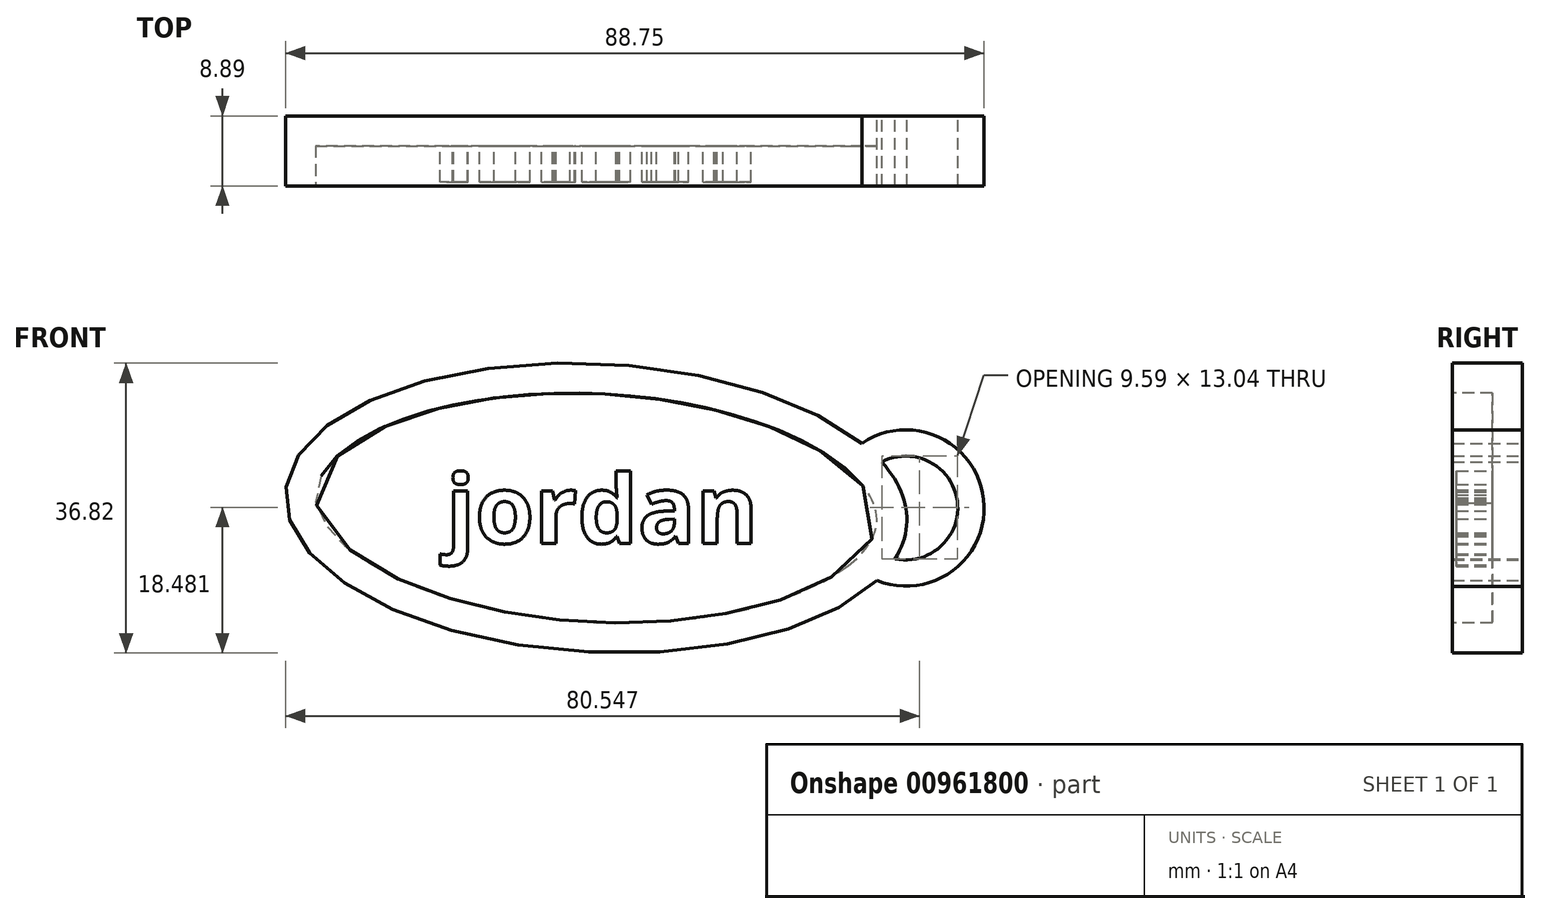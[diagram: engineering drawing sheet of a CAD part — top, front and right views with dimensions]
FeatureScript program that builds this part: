
annotation { "Feature Type Name" : "Feature", "Feature Type Description" : "" }
export const myFeature = defineFeature(function(context is Context, id is Id, definition is map)
    precondition{}
    {
        {
            var Q0;
            Q0=qCreatedBy(makeId("Front.planeOp"),FACE);
            var sketch = newSketch(context, id + "F0", { "sketchPlane" : qUnion([Q0])});
            skEllipticalArc(sketch, "E0", {});
            skArc(sketch, "E1", {"start": v(35.66, -9.23) * mm, "mid": v(49.22, 1.07) * mm, "end": v(33.76, 8.22) * mm});
            skArc(sketch, "E2", {"start": v(37.98, -6.45) * mm, "mid": v(45.87, 0.9) * mm, "end": v(36.28, 5.84) * mm});
            skEllipticalArc(sketch, "E3.trimOffspring", {});
            skFitSpline(sketch, "E4", {"points": [v(33.76, 8.22) * mm, v(36.28, 5.84) * mm], "startDerivative": vector(4.84, -3.4) * mm, "endDerivative": vector(4.84, -3.4) * mm});
            skFitSpline(sketch, "E5", {"points": [v(35.66, -9.23) * mm, v(37.98, -6.45) * mm], "startDerivative": vector(4.95, 3.83) * mm, "endDerivative": vector(4.95, 3.83) * mm});
            const initialGuessF0  = {"E0": [0, 0, 0.9988214334314441, -0.04853600846748088, 0.039509085759879645, 0.01832875752475581, 0.5672691117967682, 5.862453768805823], "E3.trimOffspring": [0, 0, 0.9988214334314441, -0.04853600846748088, 0.039509085759879645, 0.01832875752475581, 6.029563650895769, 0.4272554334626324]};
            skSetInitialGuess(sketch, initialGuessF0);
            skSolve(sketch);
        }
        {
            var Q0;
            Q0=makeQuery(id+"F0.imprint","IMPRINT",FACE,{"disambiguationData":[TD([[makeQuery(id+"F0.imprint","IMPRINT",EDGE,{"derivedFrom":sQuery(id+"F0.wireOp",EDGE,"E1")}),1.0]])]});
            var Q1;
            Q1=makeQuery(id+"F0.imprint","IMPRINT",FACE,{"disambiguationData":[TD([[makeQuery(id+"F0.imprint","IMPRINT",EDGE,{"derivedFrom":sQuery(id+"F0.wireOp",EDGE,"E0")}),1.0]])]});
            extrude(context, id + "F1", {"entities" : qUnion([Q0, Q1]), "depth" : 8.9 * mm, "offsetDistance" : 25.4 * mm});
        }
        {
            var Q0;
            Q0=makeQuery(id+"F1.opExtrude","CAP_FACE",FACE,{"disambiguationData":[OSD([sQuery(id+"F0.wireOp",EDGE,"E0"),sQuery(id+"F0.wireOp",EDGE,"E1"),sQuery(id+"F0.wireOp",EDGE,"E2"),sQuery(id+"F0.wireOp",EDGE,"E3.trimOffspring")])],"isStart":false});
            shell(context, id + "F2", {"entities" : qUnion([Q0]), "thickness" : 3.8 * mm});
        }
        {
            var Q0;
            {var subQ0=sQuery(id+"F0.wireOp",EDGE,"E3.trimOffspring");var subQ1=sQuery(id+"F0.wireOp",EDGE,"E2");var subQ2=sQuery(id+"F0.wireOp",EDGE,"E1");var subQ3=sQuery(id+"F0.wireOp",EDGE,"E0");Q0=makeQuery(id+"F2.opShell","OFFSET_FACE",FACE,{"disambiguationData":[OSD([subQ3,subQ2,subQ1,subQ0]),TDD([makeQuery(id+"F1.opExtrude","CAP_FACE",FACE,{"disambiguationData":[OSD([subQ3,subQ2,subQ1,subQ0])],"isStart":true})])]});}
            var sketch = newSketch(context, id + "F3", { "sketchPlane" : qUnion([Q0])});
            skText(sketch, "E6", { "text": "jordan\n", "fontName": "OpenSans-Bold.ttf"});
            const initialGuessF3  = {"E6": [-0.01908, -0.00448, 1, 0, 0.00873]};
            skSetInitialGuess(sketch, initialGuessF3);
            skSolve(sketch);
        }
        {
            var Q0;
            Q0 = qSketchRegion(id + "F3", true);
            extrude(context, id + "F4", {"entities" : qUnion([Q0]), "operationType" : NewBodyOperationType.ADD, "depth" : 4.57 * mm, "offsetDistance" : 25.4 * mm});
        }
    });
